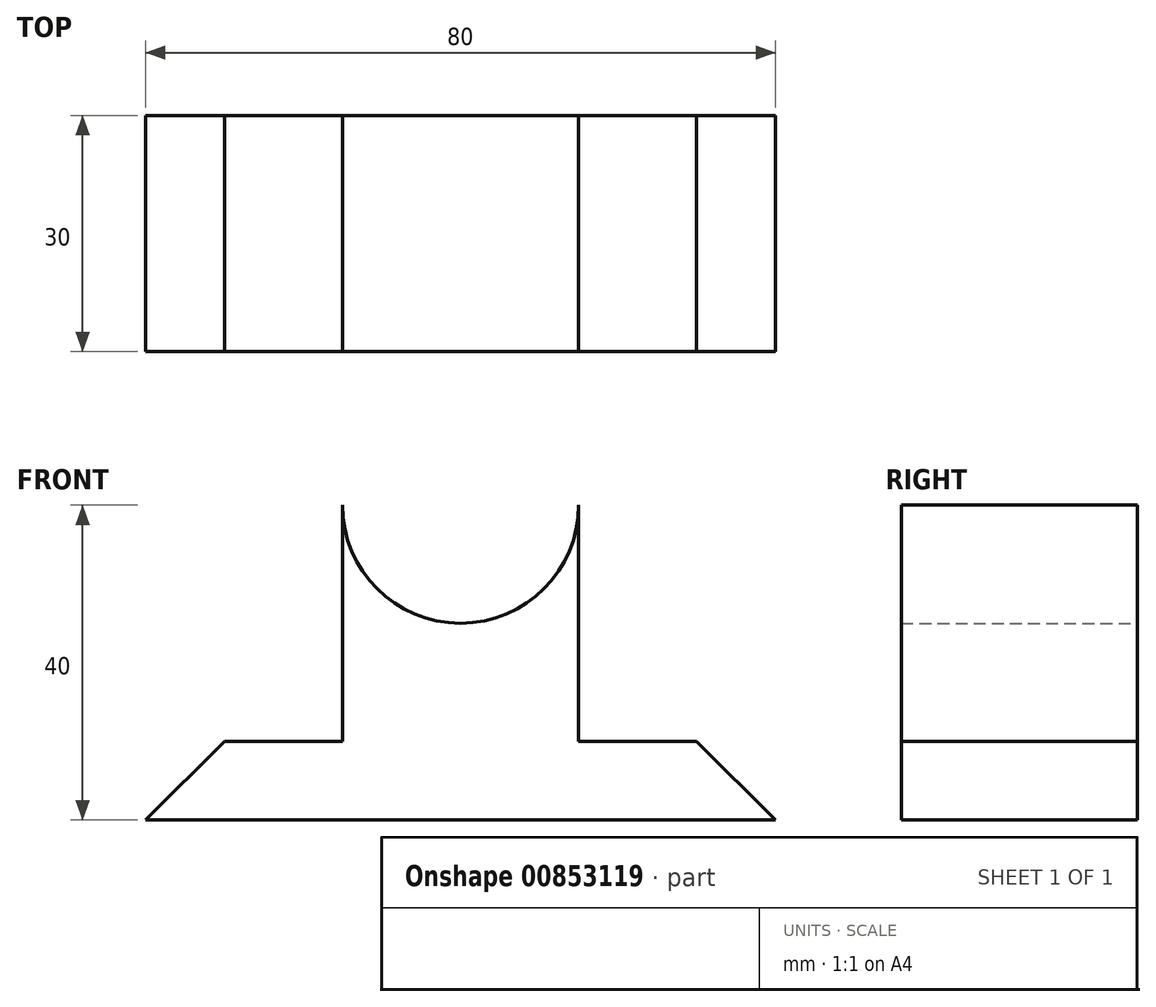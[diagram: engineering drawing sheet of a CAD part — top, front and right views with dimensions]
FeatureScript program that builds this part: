
annotation { "Feature Type Name" : "Feature", "Feature Type Description" : "" }
export const myFeature = defineFeature(function(context is Context, id is Id, definition is map)
    precondition{}
    {
        {
            var Q0;
            Q0=qCreatedBy(makeId("Top.planeOp"),FACE);
            var sketch = newSketch(context, id + "F0", { "sketchPlane" : qUnion([Q0])});
            skLineSegment(sketch, "E0.bottom", {"start": v(40, -15) * mm, "end": v(-40, -15) * mm});
            skLineSegment(sketch, "E0.top", {"start": v(40, 15) * mm, "end": v(-40, 15) * mm});
            skLineSegment(sketch, "E0.left", {"start": v(40, -15) * mm, "end": v(40, 15) * mm});
            skLineSegment(sketch, "E0.right", {"start": v(-40, -15) * mm, "end": v(-40, 15) * mm});
            skPoint(sketch, "E0.middle", {"position": v(0, 0) * mm});
            skSolve(sketch);
        }
        {
            var Q0;
            Q0=makeQuery(id+"F0.imprint","IMPRINT",FACE,{"disambiguationData":[TD([[makeQuery(id+"F0.imprint","IMPRINT",EDGE,{"derivedFrom":sQuery(id+"F0.wireOp",EDGE,"E0.bottom")}),-1.0]])]});
            extrude(context, id + "F1", {"entities" : qUnion([Q0]), "depth" : 10 * mm, "offsetDistance" : 25 * mm});
        }
        {
            var Q0;
            Q0=makeQuery(id+"F1.opExtrude","CAP_EDGE",EDGE,{"disambiguationData":[OSD([sQuery(id+"F0.wireOp",EDGE,"E0.right")])],"isStart":false});
            var Q1;
            Q1=makeQuery(id+"F1.opExtrude","CAP_EDGE",EDGE,{"disambiguationData":[OSD([sQuery(id+"F0.wireOp",EDGE,"E0.left")])],"isStart":false});
            chamfer(context, id + "F2", {"entities" : qUnion([Q0, Q1]), "width" : 10 * mm, "tangentPropagation" : true});
        }
        {
            var Q0;
            Q0=qCreatedBy(makeId("Front.planeOp"),FACE);
            var sketch = newSketch(context, id + "F3", { "sketchPlane" : qUnion([Q0])});
            skLineSegment(sketch, "E1.top", {"start": v(15, 10) * mm, "end": v(-15, 10) * mm});
            skLineSegment(sketch, "E1.left", {"start": v(15, 40) * mm, "end": v(15, 10) * mm});
            skLineSegment(sketch, "E1.right", {"start": v(-15, 40) * mm, "end": v(-15, 10) * mm});
            skPoint(sketch, "E1.middle", {"position": v(0, 25) * mm});
            skArc(sketch, "E2", {"start": v(-15, 40) * mm, "mid": v(0, 25) * mm, "end": v(15, 40) * mm});
            skSolve(sketch);
        }
        {
            var Q0;
            Q0=makeQuery(id+"F3.imprint","IMPRINT",FACE,{"disambiguationData":[TD([[makeQuery(id+"F3.imprint","IMPRINT",EDGE,{"derivedFrom":sQuery(id+"F3.wireOp",EDGE,"E1.top")}),-1.0]])]});
            extrude(context, id + "F4", {"entities" : qUnion([Q0]), "operationType" : NewBodyOperationType.ADD, "depth" : 15 * mm, "offsetDistance" : 25 * mm});
        }
        {
            var Q0;
            Q0=makeQuery(id+"F4.opExtrude","CAP_FACE",FACE,{"disambiguationData":[OSD([sQuery(id+"F3.wireOp",EDGE,"E1.top"),sQuery(id+"F3.wireOp",EDGE,"E1.left"),sQuery(id+"F3.wireOp",EDGE,"E1.right"),sQuery(id+"F3.wireOp",EDGE,"E2")])],"isStart":true});
            extrude(context, id + "F5", {"entities" : qUnion([Q0]), "operationType" : NewBodyOperationType.ADD, "depth" : 15 * mm, "offsetDistance" : 25 * mm});
        }
    });
